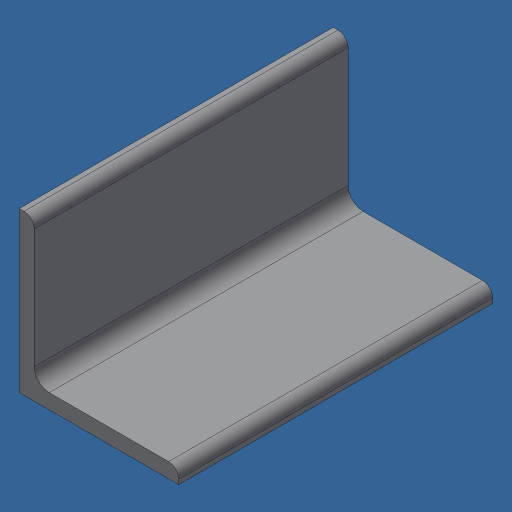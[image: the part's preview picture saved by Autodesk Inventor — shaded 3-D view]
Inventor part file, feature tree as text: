
AUTODESK INVENTOR PART (.ipt)
format: ipt  version: 2024.3 (Build 283343000, 343)  size: 111,616 bytes
history: native  units: mm (DEFAULTED — no unit token found)
features: other x1, extrude x1
ambient origin geometry x8: Origin, YZ Plane, XZ Plane, XY Plane, X Axis, Y Axis, Z Axis, Center Point
bodies: Body1 (feature_tree)
feature tree (2):
  other  "Finish - None"
  extrude  "2" X 2" X 3/16""  Depth=4.7625mm
